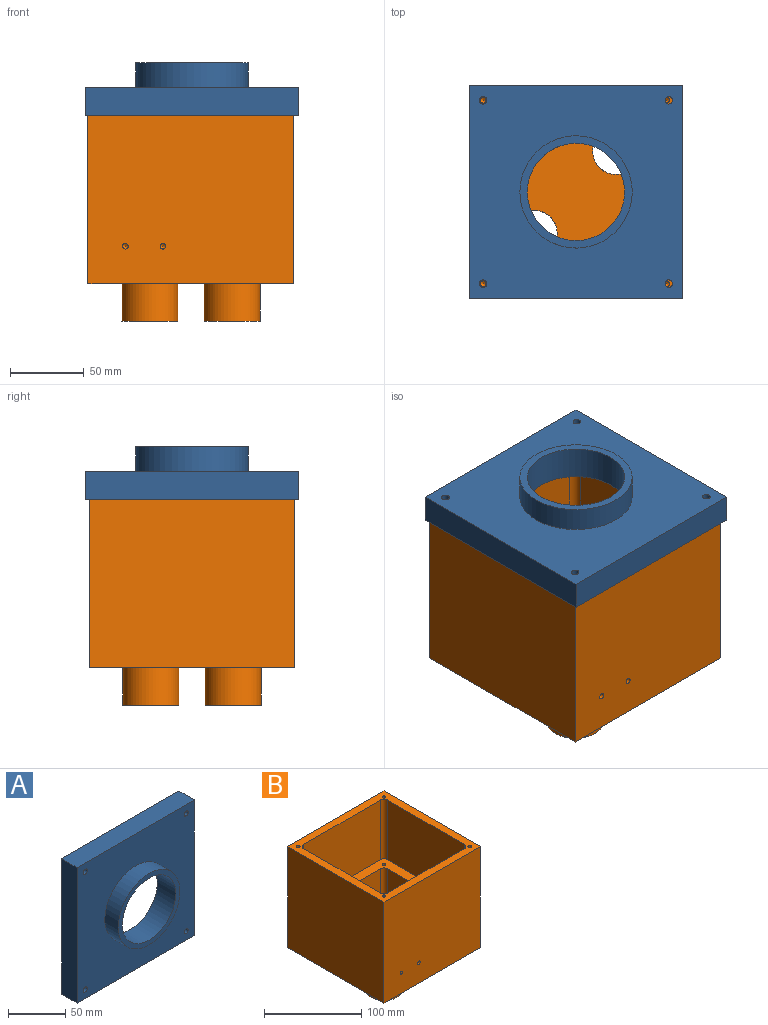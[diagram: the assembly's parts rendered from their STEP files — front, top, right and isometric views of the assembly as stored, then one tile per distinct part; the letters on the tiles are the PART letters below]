
ASSEMBLY  parts=2 mates=1
PART A: 18 faces, bbox 144.8x35.6x144.8 mm
  f0: plane 144.78x19.05mm, normal (0,0,1), area 2758.1mm2, adj f1,f3,f4,f5
  f1: plane 144.78x19.05mm, normal (-1,0,0), area 2758.1mm2, adj f0,f2,f4,f5
  f2: plane 144.78x19.05mm, normal (0,0,-1), area 2758.1mm2, adj f1,f3,f4,f5
  f3: plane 144.78x19.05mm, normal (1,0,0), area 2758.1mm2, adj f0,f2,f4,f5
  f4: plane 144.78x144.78mm, normal (0,-1,0), area 16319mm2, adj f0,f1,f2,f3,f11,f14,f15,f16
  f5: plane 144.78x144.78mm, normal (0,1,0), area 1045.4mm2, adj f0,f1,f2,f3,f6,f7,f8,f9
  f6: plane 141.92x12.7mm, normal (-1,0,0), area 1802.3mm2, adj f5,f7,f9,f10
  f7: plane 140.34x12.7mm, normal (0,0,-1), area 1782.3mm2, adj f5,f6,f8,f10
  f8: plane 141.92x12.7mm, normal (1,0,0), area 1802.3mm2, adj f5,f7,f9,f10
  f9: plane 140.34x12.7mm, normal (0,0,1), area 1782.3mm2, adj f5,f6,f8,f10
  f10: plane 141.92x140.34mm, normal (0,1,0), area 16408.6mm2, adj f6,f7,f8,f9,f13,f14,f15,f16
  f11: cylinder r=38.1mm len=76.2mm, axis (0,1,0), area 3952.3mm2, adj f4,f12
  f12: plane 76.2x76.2mm, normal (0,-1,0), area 1135mm2, adj f11,f13
  f13: cylinder r=33.02mm len=66.04mm, axis (0,-1,0), area 4742.8mm2, adj f10,f12
  f14: cylinder r=2.55mm len=6.35mm, axis (0,-1,0), area 101.8mm2, adj f4,f10
  f15: cylinder r=2.55mm len=6.35mm, axis (0,-1,0), area 101.8mm2, adj f4,f10
  f16: cylinder r=2.55mm len=6.35mm, axis (0,-1,0), area 101.8mm2, adj f4,f10
  f17: cylinder r=2.55mm len=6.35mm, axis (0,-1,0), area 101.8mm2, adj f4,f10
PART B: 54 faces, bbox 139.7x139.7x152.4 mm
  f0: plane 111.76x74.93mm, normal (0,-1,0), area 8374.2mm2, adj f4,f14,f34,f37
  f1: plane 111.76x74.93mm, normal (1,0,0), area 8374.2mm2, adj f4,f14,f34,f35
  f2: plane 111.76x74.93mm, normal (0,1,0), area 8374.2mm2, adj f4,f14,f35,f36
  f3: plane 111.76x74.93mm, normal (-1,0,0), area 8374.2mm2, adj f4,f14,f36,f37
  f4: plane 139.7x139.7mm, normal (0,0,1), area 4628.5mm2, adj f0,f1,f2,f3,f5,f6,f7,f8
  f5: plane 139.7x127mm, normal (0,1,0), area 17719.2mm2, adj f4,f6,f8,f9,f51,f53
  f6: plane 139.7x127mm, normal (-1,0,0), area 17741.9mm2, adj f4,f5,f7,f9
  f7: plane 139.7x127mm, normal (0,-1,0), area 17719.2mm2, adj f4,f6,f8,f9,f47,f49
  f8: plane 139.7x127mm, normal (1,0,0), area 17741.9mm2, adj f4,f5,f7,f9
  f9: plane 139.7x139.7mm, normal (0,0,-1), area 17235.9mm2, adj f5,f6,f7,f8,f24,f26
  f10: plane 88.9x44.45mm, normal (1,0,0), area 3951.6mm2, adj f14,f15,f30,f33
  f11: plane 88.9x44.45mm, normal (0,-1,0), area 3951.6mm2, adj f14,f15,f30,f31
  f12: plane 88.9x44.45mm, normal (-1,0,0), area 3951.6mm2, adj f14,f15,f31,f32
  f13: plane 88.9x44.45mm, normal (0,1,0), area 3951.6mm2, adj f14,f15,f32,f33
  f14: plane 121.92x121.92mm, normal (0,0,1), area 5006.3mm2, adj f0,f1,f2,f3,f10,f11,f12,f13
  f15: plane 99.06x99.06mm, normal (0,0,1), area 8207.3mm2, adj f10,f11,f12,f13,f28,f29,f30,f31
  f16: cone r=0mm half-angle=59deg, axis (0,0,1), area 13.2mm2, adj f17
  f17: cylinder r=1.9mm len=12.7mm, axis (0,0,1), area 151.5mm2, adj f14,f16
  f18: cone r=0mm half-angle=59deg, axis (0,0,1), area 13.2mm2, adj f19
  f19: cylinder r=1.9mm len=12.7mm, axis (0,0,1), area 151.5mm2, adj f14,f18
  f20: cone r=0mm half-angle=59deg, axis (0,0,1), area 13.2mm2, adj f21
  f21: cylinder r=1.9mm len=12.7mm, axis (0,0,1), area 151.5mm2, adj f14,f20
  f22: cone r=0mm half-angle=59deg, axis (0,0,1), area 13.2mm2, adj f23
  f23: cylinder r=1.9mm len=12.7mm, axis (0,0,1), area 151.5mm2, adj f14,f22
  f24: cylinder r=19.05mm len=38.1mm, axis (0,0,1), area 3040.2mm2, adj f9,f25
  f25: plane 38.1x38.1mm, normal (0,0,-1), area 348.4mm2, adj f24,f29
  f26: cylinder r=19.05mm len=38.1mm, axis (0,0,1), area 3040.2mm2, adj f9,f27
  f27: plane 38.1x38.1mm, normal (0,0,-1), area 348.4mm2, adj f26,f28
  f28: cylinder r=15.88mm len=33.02mm, axis (0,0,-1), area 3293.6mm2, adj f15,f27
  f29: cylinder r=15.88mm len=33.02mm, axis (0,0,-1), area 3293.6mm2, adj f15,f25
  f30: cylinder r=5.08mm len=44.45mm, axis (0,0,-1), area 354.7mm2, adj f10,f11,f14,f15
  f31: cylinder r=5.08mm len=44.45mm, axis (0,0,1), area 354.7mm2, adj f11,f12,f14,f15
  f32: cylinder r=5.08mm len=44.45mm, axis (0,0,-1), area 354.7mm2, adj f12,f13,f14,f15
  f33: cylinder r=5.08mm len=44.45mm, axis (0,0,1), area 354.7mm2, adj f10,f13,f14,f15
  f34: cylinder r=5.08mm len=74.93mm, axis (0,0,1), area 597.9mm2, adj f0,f1,f4,f14
  f35: cylinder r=5.08mm len=74.93mm, axis (0,0,-1), area 597.9mm2, adj f1,f2,f4,f14
  f36: cylinder r=5.08mm len=74.93mm, axis (0,0,1), area 597.9mm2, adj f2,f3,f4,f14
  f37: cylinder r=5.08mm len=74.93mm, axis (0,0,-1), area 597.9mm2, adj f0,f3,f4,f14
  f38: cone r=0mm half-angle=59deg, axis (0,0,1), area 13.2mm2, adj f39
  f39: cylinder r=1.9mm len=12.7mm, axis (0,0,1), area 151.5mm2, adj f4,f38
  f40: cone r=0mm half-angle=59deg, axis (0,0,1), area 13.2mm2, adj f41
  f41: cylinder r=1.9mm len=12.7mm, axis (0,0,1), area 151.5mm2, adj f4,f40
  f42: cone r=0mm half-angle=59deg, axis (0,0,1), area 13.2mm2, adj f43
  f43: cylinder r=1.9mm len=12.7mm, axis (0,0,1), area 151.5mm2, adj f4,f42
  f44: cone r=0mm half-angle=59deg, axis (0,0,1), area 13.2mm2, adj f45
  f45: cylinder r=1.9mm len=12.7mm, axis (0,0,1), area 151.5mm2, adj f4,f44
  f46: cone r=0mm half-angle=59deg, axis (0,-1,0), area 13.2mm2, adj f47
  f47: cylinder r=1.9mm len=12.7mm, axis (0,-1,0), area 151.5mm2, adj f7,f46
  f48: cone r=0mm half-angle=59deg, axis (0,-1,0), area 13.2mm2, adj f49
  f49: cylinder r=1.9mm len=12.7mm, axis (0,-1,0), area 151.5mm2, adj f7,f48
  f50: cone r=0mm half-angle=59deg, axis (0,1,0), area 13.2mm2, adj f51
  f51: cylinder r=1.9mm len=12.7mm, axis (0,1,0), area 151.5mm2, adj f5,f50
  f52: cone r=0mm half-angle=59deg, axis (0,1,0), area 13.2mm2, adj f53
  f53: cylinder r=1.9mm len=12.7mm, axis (0,1,0), area 151.5mm2, adj f5,f52
PLACE A rot(axis=(-0.58,0.58,-0.58),120deg) t=(1.68,-0.71,67.98)mm
PLACE B t=(0.93,-0.71,-46.32)mm
MATE fastened A.f17 <-> B.f38  axis (0,0,-1) through (-61.3,61.52,80.68)mm
